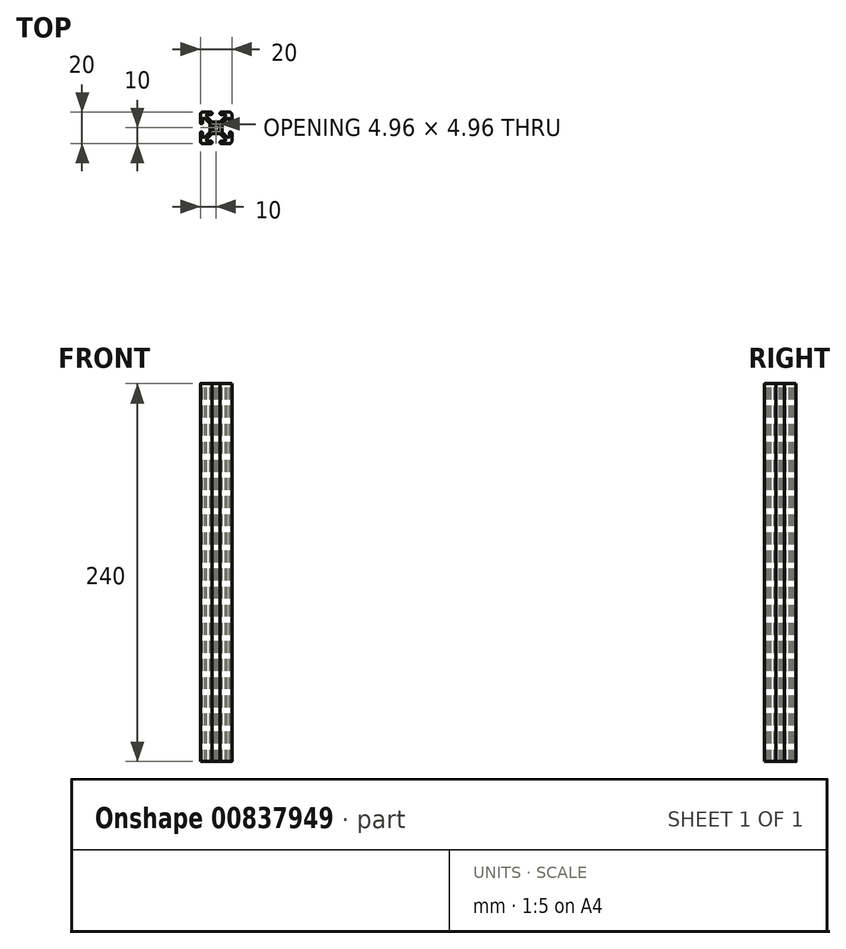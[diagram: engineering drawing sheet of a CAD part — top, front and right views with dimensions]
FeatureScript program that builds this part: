
annotation { "Feature Type Name" : "Feature", "Feature Type Description" : "" }
export const myFeature = defineFeature(function(context is Context, id is Id, definition is map)
    precondition{}
    {
        {
            var Q0;
            Q0=qCreatedBy(makeId("Top.planeOp"),FACE);
            var sketch = newSketch(context, id + "F0", { "sketchPlane" : qUnion([Q0])});
            skLineSegment(sketch, "E0.bottom", {"start": v(10, 10) * mm, "end": v(-10, 10) * mm});
            skLineSegment(sketch, "E0.top", {"start": v(10, -10) * mm, "end": v(-10, -10) * mm});
            skLineSegment(sketch, "E0.left", {"start": v(10, 10) * mm, "end": v(10, -10) * mm});
            skLineSegment(sketch, "E0.right", {"start": v(-10, 10) * mm, "end": v(-10, -10) * mm});
            skPoint(sketch, "E0.middle", {"position": v(0, 0) * mm});
            skCircle(sketch, "E1", {"center": v(0, 0) * mm, "radius": 2.1 * mm});
            skCircle(sketch, "E2", {"center": v(1.48, 1.48) * mm, "radius": 1 * mm});
            skLineSegment(sketch, "E3", {"start": v(0, 0) * mm, "end": v(1.48, 1.48) * mm, "construction": true});
            skLineSegment(sketch, "E4.bottom", {"start": v(-3.65, 3.65) * mm, "end": v(3.65, 3.65) * mm});
            skLineSegment(sketch, "E4.top", {"start": v(-3.65, -3.65) * mm, "end": v(3.65, -3.65) * mm});
            skLineSegment(sketch, "E4.left", {"start": v(-3.65, 3.65) * mm, "end": v(-3.65, -3.65) * mm});
            skLineSegment(sketch, "E4.right", {"start": v(3.65, 3.65) * mm, "end": v(3.65, -3.65) * mm});
            skCircle(sketch, "E5.1.0", {"center": v(-1.48, 1.48) * mm, "radius": 1 * mm});
            skCircle(sketch, "E5.2.0", {"center": v(-1.48, -1.48) * mm, "radius": 1 * mm});
            skCircle(sketch, "E5.3.0", {"center": v(1.48, -1.48) * mm, "radius": 1 * mm});
            skLineSegment(sketch, "E6.bottom", {"start": v(-8.5, 8.5) * mm, "end": v(8.5, 8.5) * mm});
            skLineSegment(sketch, "E6.top", {"start": v(-8.5, -8.5) * mm, "end": v(8.5, -8.5) * mm});
            skLineSegment(sketch, "E6.left", {"start": v(-8.5, 8.5) * mm, "end": v(-8.5, -8.5) * mm});
            skLineSegment(sketch, "E6.right", {"start": v(8.5, 8.5) * mm, "end": v(8.5, -8.5) * mm});
            skLineSegment(sketch, "E7", {"start": v(7.44, 8.5) * mm, "end": v(-8.5, -7.44) * mm});
            skLineSegment(sketch, "E8", {"start": v(-7.44, -8.5) * mm, "end": v(8.5, 7.44) * mm});
            skLineSegment(sketch, "E9", {"start": v(-8.5, 7.44) * mm, "end": v(7.44, -8.5) * mm});
            skLineSegment(sketch, "E10", {"start": v(8.5, -7.44) * mm, "end": v(-7.44, 8.5) * mm});
            skLineSegment(sketch, "E11", {"start": v(-10, 2.6) * mm, "end": v(-8.5, 2.6) * mm});
            skLineSegment(sketch, "E12", {"start": v(-10, -2.6) * mm, "end": v(-8.5, -2.6) * mm});
            skLineSegment(sketch, "E13", {"start": v(8.5, 2.6) * mm, "end": v(10, 2.6) * mm});
            skLineSegment(sketch, "E14", {"start": v(8.5, -2.6) * mm, "end": v(10, -2.6) * mm});
            skLineSegment(sketch, "E15", {"start": v(-2.6, 8.5) * mm, "end": v(-2.6, 10) * mm});
            skLineSegment(sketch, "E16", {"start": v(2.6, 8.5) * mm, "end": v(2.6, 10) * mm});
            skLineSegment(sketch, "E17", {"start": v(-2.6, -8.5) * mm, "end": v(-2.6, -10) * mm});
            skPoint(sketch, "E18.endSnap0", {"position": v(0, -10) * mm});
            skLineSegment(sketch, "E19", {"start": v(2.6, -8.5) * mm, "end": v(2.6, -10) * mm});
            skLineSegment(sketch, "E20", {"start": v(-8.5, 6) * mm, "end": v(-7.06, 6) * mm});
            skLineSegment(sketch, "E21", {"start": v(-6, 7.06) * mm, "end": v(-6, 8.5) * mm});
            skLineSegment(sketch, "E22", {"start": v(6, 8.5) * mm, "end": v(6, 7.06) * mm});
            skLineSegment(sketch, "E23", {"start": v(8.5, 6) * mm, "end": v(7.06, 6) * mm});
            skLineSegment(sketch, "E24", {"start": v(8.5, -6) * mm, "end": v(7.06, -6) * mm});
            skLineSegment(sketch, "E25", {"start": v(6, -8.5) * mm, "end": v(6, -7.06) * mm});
            skLineSegment(sketch, "E26", {"start": v(-6, -8.5) * mm, "end": v(-6, -7.06) * mm});
            skLineSegment(sketch, "E27", {"start": v(-7.06, -6) * mm, "end": v(-8.5, -6) * mm});
            skSolve(sketch);
        }
        {
            var Q0;
            {var subQ8=sQuery(id+"F0.wireOp",EDGE,"E11");Q0=makeQuery(id+"F0.imprint","IMPRINT",FACE,{"disambiguationData":[TD([[makeQuery(id+"F0.imprint","IMPRINT",EDGE,{"derivedFrom":subQ8}),1.0]])]});}
            var Q1;
            {var subQ3=sQuery(id+"F0.wireOp",EDGE,"E20");Q1=makeQuery(id+"F0.imprint","IMPRINT",FACE,{"disambiguationData":[TD([[makeQuery(id+"F0.imprint","IMPRINT",EDGE,{"derivedFrom":subQ3}),1.0]])]});}
            var Q2;
            {var subQ3=sQuery(id+"F0.wireOp",EDGE,"E21");Q2=makeQuery(id+"F0.imprint","IMPRINT",FACE,{"disambiguationData":[TD([[makeQuery(id+"F0.imprint","IMPRINT",EDGE,{"derivedFrom":subQ3}),1.0]])]});}
            var Q3;
            {var subQ5=sQuery(id+"F0.wireOp",EDGE,"E4.left");var subQ6=sQuery(id+"F0.wireOp",EDGE,"E4.bottom");var subQ7=makeQuery(id+"F0.imprint","INTERSECT",VERTEX,{"derivedFrom":[subQ6,subQ5]});Q3=makeQuery(id+"F0.imprint","IMPRINT",FACE,{"disambiguationData":[TD([[makeQuery(id+"F0.imprint","IMPRINT",EDGE,{"disambiguationData":[TD([[subQ7,-1.0]])],"derivedFrom":subQ6}),1.0]])]});}
            var Q4;
            {var subQ3=sQuery(id+"F0.wireOp",EDGE,"E13");Q4=makeQuery(id+"F0.imprint","IMPRINT",FACE,{"disambiguationData":[TD([[makeQuery(id+"F0.imprint","IMPRINT",EDGE,{"derivedFrom":subQ3}),1.0]])]});}
            var Q5;
            {var subQ3=sQuery(id+"F0.wireOp",EDGE,"E22");Q5=makeQuery(id+"F0.imprint","IMPRINT",FACE,{"disambiguationData":[TD([[makeQuery(id+"F0.imprint","IMPRINT",EDGE,{"derivedFrom":subQ3}),1.0]])]});}
            var Q6;
            {var subQ8=sQuery(id+"F0.wireOp",EDGE,"E4.right");var subQ9=sQuery(id+"F0.wireOp",EDGE,"E4.bottom");var subQ10=makeQuery(id+"F0.imprint","INTERSECT",VERTEX,{"derivedFrom":[subQ9,subQ8]});Q6=makeQuery(id+"F0.imprint","IMPRINT",FACE,{"disambiguationData":[TD([[makeQuery(id+"F0.imprint","IMPRINT",EDGE,{"disambiguationData":[TD([[subQ10,1.0]])],"derivedFrom":subQ9}),1.0]])]});}
            var Q7;
            {var subQ3=sQuery(id+"F0.wireOp",EDGE,"E23");Q7=makeQuery(id+"F0.imprint","IMPRINT",FACE,{"disambiguationData":[TD([[makeQuery(id+"F0.imprint","IMPRINT",EDGE,{"derivedFrom":subQ3}),-1.0]])]});}
            var Q8;
            {var subQ3=sQuery(id+"F0.wireOp",EDGE,"E25");Q8=makeQuery(id+"F0.imprint","IMPRINT",FACE,{"disambiguationData":[TD([[makeQuery(id+"F0.imprint","IMPRINT",EDGE,{"derivedFrom":subQ3}),-1.0]])]});}
            var Q9;
            {var subQ8=sQuery(id+"F0.wireOp",EDGE,"E4.right");var subQ10=sQuery(id+"F0.wireOp",EDGE,"E4.top");var subQ11=makeQuery(id+"F0.imprint","INTERSECT",VERTEX,{"derivedFrom":[subQ10,subQ8]});Q9=makeQuery(id+"F0.imprint","IMPRINT",FACE,{"disambiguationData":[TD([[makeQuery(id+"F0.imprint","IMPRINT",EDGE,{"disambiguationData":[TD([[subQ11,1.0]])],"derivedFrom":subQ10}),-1.0]])]});}
            var Q10;
            {var subQ3=sQuery(id+"F0.wireOp",EDGE,"E24");Q10=makeQuery(id+"F0.imprint","IMPRINT",FACE,{"disambiguationData":[TD([[makeQuery(id+"F0.imprint","IMPRINT",EDGE,{"derivedFrom":subQ3}),1.0]])]});}
            var Q11;
            {var subQ7=sQuery(id+"F0.wireOp",EDGE,"E14");Q11=makeQuery(id+"F0.imprint","IMPRINT",FACE,{"disambiguationData":[TD([[makeQuery(id+"F0.imprint","IMPRINT",EDGE,{"derivedFrom":subQ7}),-1.0]])]});}
            var Q12;
            {var subQ11=sQuery(id+"F0.wireOp",EDGE,"E12");Q12=makeQuery(id+"F0.imprint","IMPRINT",FACE,{"disambiguationData":[TD([[makeQuery(id+"F0.imprint","IMPRINT",EDGE,{"derivedFrom":subQ11}),-1.0]])]});}
            var Q13;
            {var subQ3=sQuery(id+"F0.wireOp",EDGE,"E26");Q13=makeQuery(id+"F0.imprint","IMPRINT",FACE,{"disambiguationData":[TD([[makeQuery(id+"F0.imprint","IMPRINT",EDGE,{"derivedFrom":subQ3}),1.0]])]});}
            var Q14;
            {var subQ3=sQuery(id+"F0.wireOp",EDGE,"E27");Q14=makeQuery(id+"F0.imprint","IMPRINT",FACE,{"disambiguationData":[TD([[makeQuery(id+"F0.imprint","IMPRINT",EDGE,{"derivedFrom":subQ3}),1.0]])]});}
            var Q15;
            {var subQ7=sQuery(id+"F0.wireOp",EDGE,"E4.top");var subQ11=sQuery(id+"F0.wireOp",EDGE,"E4.left");var subQ12=makeQuery(id+"F0.imprint","INTERSECT",VERTEX,{"derivedFrom":[subQ7,subQ11]});Q15=makeQuery(id+"F0.imprint","IMPRINT",FACE,{"disambiguationData":[TD([[makeQuery(id+"F0.imprint","IMPRINT",EDGE,{"disambiguationData":[TD([[subQ12,-1.0]])],"derivedFrom":subQ7}),-1.0]])]});}
            var Q16;
            {var subQ1=sQuery(id+"F0.wireOp",EDGE,"E4.left");var subQ7=sQuery(id+"F0.wireOp",EDGE,"E4.top");var subQ8=makeQuery(id+"F0.imprint","INTERSECT",VERTEX,{"derivedFrom":[subQ7,subQ1]});Q16=makeQuery(id+"F0.imprint","IMPRINT",FACE,{"disambiguationData":[TD([[makeQuery(id+"F0.imprint","IMPRINT",EDGE,{"disambiguationData":[TD([[subQ8,-1.0]])],"derivedFrom":subQ7}),1.0]])]});}
            var Q17;
            {var subQ1=sQuery(id+"F0.wireOp",EDGE,"E1");var subQ7=sQuery(id+"F0.wireOp",EDGE,"E5.2.0");var subQ8=makeQuery(id+"F0.imprint","INTERSECT",VERTEX,{"disambiguationData":[OD(1.0)],"derivedFrom":[subQ1,subQ7]});Q17=makeQuery(id+"F0.imprint","IMPRINT",FACE,{"disambiguationData":[TD([[makeQuery(id+"F0.imprint","IMPRINT",EDGE,{"disambiguationData":[TD([[subQ8,-1.0]])],"derivedFrom":subQ1}),-1.0]])]});}
            var Q18;
            {var subQ1=sQuery(id+"F0.wireOp",EDGE,"E4.top");var subQ7=sQuery(id+"F0.wireOp",EDGE,"E4.right");var subQ8=makeQuery(id+"F0.imprint","INTERSECT",VERTEX,{"derivedFrom":[subQ1,subQ7]});Q18=makeQuery(id+"F0.imprint","IMPRINT",FACE,{"disambiguationData":[TD([[makeQuery(id+"F0.imprint","IMPRINT",EDGE,{"disambiguationData":[TD([[subQ8,1.0]])],"derivedFrom":subQ1}),1.0]])]});}
            var Q19;
            {var subQ1=sQuery(id+"F0.wireOp",EDGE,"E1");var subQ9=sQuery(id+"F0.wireOp",EDGE,"E2");var subQ10=makeQuery(id+"F0.imprint","INTERSECT",VERTEX,{"disambiguationData":[OD(0.0)],"derivedFrom":[subQ1,subQ9]});Q19=makeQuery(id+"F0.imprint","IMPRINT",FACE,{"disambiguationData":[TD([[makeQuery(id+"F0.imprint","IMPRINT",EDGE,{"disambiguationData":[TD([[subQ10,1.0]])],"derivedFrom":subQ1}),-1.0]])]});}
            var Q20;
            {var subQ0=sQuery(id+"F0.wireOp",EDGE,"E7");var subQ1=sQuery(id+"F0.wireOp",EDGE,"E2");var subQ2=makeQuery(id+"F0.imprint","INTERSECT",VERTEX,{"disambiguationData":[OD(0.0)],"derivedFrom":[subQ1,subQ0]});Q20=makeQuery(id+"F0.imprint","IMPRINT",FACE,{"disambiguationData":[TD([[makeQuery(id+"F0.imprint","IMPRINT",EDGE,{"disambiguationData":[TD([[subQ2,1.0]])],"derivedFrom":subQ1}),-1.0]])]});}
            var Q21;
            {var subQ0=sQuery(id+"F0.wireOp",EDGE,"E2");var subQ1=sQuery(id+"F0.wireOp",EDGE,"E1");var subQ2=makeQuery(id+"F0.imprint","INTERSECT",VERTEX,{"disambiguationData":[OD(1.0)],"derivedFrom":[subQ1,subQ0]});Q21=makeQuery(id+"F0.imprint","IMPRINT",FACE,{"disambiguationData":[TD([[makeQuery(id+"F0.imprint","IMPRINT",EDGE,{"disambiguationData":[TD([[subQ2,-1.0]])],"derivedFrom":subQ1}),-1.0]])]});}
            var Q22;
            {var subQ5=sQuery(id+"F0.wireOp",EDGE,"E4.left");var subQ6=sQuery(id+"F0.wireOp",EDGE,"E4.bottom");var subQ7=makeQuery(id+"F0.imprint","INTERSECT",VERTEX,{"derivedFrom":[subQ6,subQ5]});Q22=makeQuery(id+"F0.imprint","IMPRINT",FACE,{"disambiguationData":[TD([[makeQuery(id+"F0.imprint","IMPRINT",EDGE,{"disambiguationData":[TD([[subQ7,-1.0]])],"derivedFrom":subQ6}),-1.0]])]});}
            var Q23;
            {var subQ1=sQuery(id+"F0.wireOp",EDGE,"E1");var subQ5=sQuery(id+"F0.wireOp",EDGE,"E5.1.0");var subQ6=makeQuery(id+"F0.imprint","INTERSECT",VERTEX,{"disambiguationData":[OD(1.0)],"derivedFrom":[subQ1,subQ5]});Q23=makeQuery(id+"F0.imprint","IMPRINT",FACE,{"disambiguationData":[TD([[makeQuery(id+"F0.imprint","IMPRINT",EDGE,{"disambiguationData":[TD([[subQ6,-1.0]])],"derivedFrom":subQ1}),-1.0]])]});}
            extrude(context, id + "F1", {"entities" : qUnion([Q0, Q1, Q2, Q3, Q4, Q5, Q6, Q7, Q8, Q9, Q10, Q11, Q12, Q13, Q14, Q15, Q16, Q17, Q18, Q19, Q20, Q21, Q22, Q23]), "depth" : -240 * mm, "offsetDistance" : 25 * mm});
        }
        {
            var Q0;
            Q0=makeQuery(id+"F1.opExtrude","SWEPT_EDGE",EDGE,{"disambiguationData":[OSD([sQuery(id+"F0.wireOp",EDGE,"E0.top"),sQuery(id+"F0.wireOp",EDGE,"E0.right")])]});
            var Q1;
            Q1=makeQuery(id+"F1.opExtrude","SWEPT_EDGE",EDGE,{"disambiguationData":[OSD([sQuery(id+"F0.wireOp",EDGE,"E0.bottom"),sQuery(id+"F0.wireOp",EDGE,"E0.right")])]});
            var Q2;
            Q2=makeQuery(id+"F1.opExtrude","SWEPT_EDGE",EDGE,{"disambiguationData":[OSD([sQuery(id+"F0.wireOp",EDGE,"E0.top"),sQuery(id+"F0.wireOp",EDGE,"E0.left")])]});
            var Q3;
            Q3=makeQuery(id+"F1.opExtrude","SWEPT_EDGE",EDGE,{"disambiguationData":[OSD([sQuery(id+"F0.wireOp",EDGE,"E0.bottom"),sQuery(id+"F0.wireOp",EDGE,"E0.left")])]});
            fillet(context, id + "F2", {"entities" : qUnion([Q0, Q1, Q2, Q3]), "radius" : 1.5 * mm, "tangentPropagation" : true, "allowEdgeOverflow" : false});
        }
        {
            var Q0;
            Q0=makeQuery(id+"F1.opExtrude","SWEPT_EDGE",EDGE,{"disambiguationData":[OSD([sQuery(id+"F0.wireOp",EDGE,"E6.top"),sQuery(id+"F0.wireOp",EDGE,"E26")])]});
            var Q1;
            Q1=makeQuery(id+"F1.opExtrude","SWEPT_EDGE",EDGE,{"disambiguationData":[OSD([sQuery(id+"F0.wireOp",EDGE,"E6.left"),sQuery(id+"F0.wireOp",EDGE,"E27")])]});
            var Q2;
            Q2=makeQuery(id+"F1.opExtrude","SWEPT_EDGE",EDGE,{"disambiguationData":[OSD([sQuery(id+"F0.wireOp",EDGE,"E6.left"),sQuery(id+"F0.wireOp",EDGE,"E20")])]});
            var Q3;
            Q3=makeQuery(id+"F1.opExtrude","SWEPT_EDGE",EDGE,{"disambiguationData":[OSD([sQuery(id+"F0.wireOp",EDGE,"E6.bottom"),sQuery(id+"F0.wireOp",EDGE,"E21")])]});
            var Q4;
            Q4=makeQuery(id+"F1.opExtrude","SWEPT_EDGE",EDGE,{"disambiguationData":[OSD([sQuery(id+"F0.wireOp",EDGE,"E6.top"),sQuery(id+"F0.wireOp",EDGE,"E25")])]});
            var Q5;
            Q5=makeQuery(id+"F1.opExtrude","SWEPT_EDGE",EDGE,{"disambiguationData":[OSD([sQuery(id+"F0.wireOp",EDGE,"E6.right"),sQuery(id+"F0.wireOp",EDGE,"E24")])]});
            var Q6;
            Q6=makeQuery(id+"F1.opExtrude","SWEPT_EDGE",EDGE,{"disambiguationData":[OSD([sQuery(id+"F0.wireOp",EDGE,"E6.right"),sQuery(id+"F0.wireOp",EDGE,"E23")])]});
            var Q7;
            Q7=makeQuery(id+"F1.opExtrude","SWEPT_EDGE",EDGE,{"disambiguationData":[OSD([sQuery(id+"F0.wireOp",EDGE,"E6.bottom"),sQuery(id+"F0.wireOp",EDGE,"E22")])]});
            var Q8;
            Q8=makeQuery(id+"F1.opExtrude","SWEPT_EDGE",EDGE,{"disambiguationData":[OSD([sQuery(id+"F0.wireOp",EDGE,"E0.bottom"),sQuery(id+"F0.wireOp",EDGE,"E15")])]});
            var Q9;
            Q9=makeQuery(id+"F1.opExtrude","SWEPT_EDGE",EDGE,{"disambiguationData":[OSD([sQuery(id+"F0.wireOp",EDGE,"E6.bottom"),sQuery(id+"F0.wireOp",EDGE,"E15")])]});
            var Q10;
            Q10=makeQuery(id+"F1.opExtrude","SWEPT_EDGE",EDGE,{"disambiguationData":[OSD([sQuery(id+"F0.wireOp",EDGE,"E0.bottom"),sQuery(id+"F0.wireOp",EDGE,"E16")])]});
            var Q11;
            Q11=makeQuery(id+"F1.opExtrude","SWEPT_EDGE",EDGE,{"disambiguationData":[OSD([sQuery(id+"F0.wireOp",EDGE,"E6.left"),sQuery(id+"F0.wireOp",EDGE,"E11")])]});
            var Q12;
            Q12=makeQuery(id+"F1.opExtrude","SWEPT_EDGE",EDGE,{"disambiguationData":[OSD([sQuery(id+"F0.wireOp",EDGE,"E6.left"),sQuery(id+"F0.wireOp",EDGE,"E12")])]});
            var Q13;
            Q13=makeQuery(id+"F1.opExtrude","SWEPT_EDGE",EDGE,{"disambiguationData":[OSD([sQuery(id+"F0.wireOp",EDGE,"E0.right"),sQuery(id+"F0.wireOp",EDGE,"E12")])]});
            var Q14;
            Q14=makeQuery(id+"F1.opExtrude","SWEPT_EDGE",EDGE,{"disambiguationData":[OSD([sQuery(id+"F0.wireOp",EDGE,"E6.top"),sQuery(id+"F0.wireOp",EDGE,"E17")])]});
            var Q15;
            Q15=makeQuery(id+"F1.opExtrude","SWEPT_EDGE",EDGE,{"disambiguationData":[OSD([sQuery(id+"F0.wireOp",EDGE,"E0.top"),sQuery(id+"F0.wireOp",EDGE,"E17")])]});
            var Q16;
            Q16=makeQuery(id+"F1.opExtrude","SWEPT_EDGE",EDGE,{"disambiguationData":[OSD([sQuery(id+"F0.wireOp",EDGE,"E6.top"),sQuery(id+"F0.wireOp",EDGE,"E19")])]});
            var Q17;
            Q17=makeQuery(id+"F1.opExtrude","SWEPT_EDGE",EDGE,{"disambiguationData":[OSD([sQuery(id+"F0.wireOp",EDGE,"E6.right"),sQuery(id+"F0.wireOp",EDGE,"E14")])]});
            var Q18;
            Q18=makeQuery(id+"F1.opExtrude","SWEPT_EDGE",EDGE,{"disambiguationData":[OSD([sQuery(id+"F0.wireOp",EDGE,"E0.left"),sQuery(id+"F0.wireOp",EDGE,"E14")])]});
            var Q19;
            Q19=makeQuery(id+"F1.opExtrude","SWEPT_EDGE",EDGE,{"disambiguationData":[OSD([sQuery(id+"F0.wireOp",EDGE,"E0.left"),sQuery(id+"F0.wireOp",EDGE,"E13")])]});
            var Q20;
            Q20=makeQuery(id+"F1.opExtrude","SWEPT_EDGE",EDGE,{"disambiguationData":[OSD([sQuery(id+"F0.wireOp",EDGE,"E6.right"),sQuery(id+"F0.wireOp",EDGE,"E13")])]});
            var Q21;
            Q21=makeQuery(id+"F1.opExtrude","SWEPT_EDGE",EDGE,{"disambiguationData":[OSD([sQuery(id+"F0.wireOp",EDGE,"E6.bottom"),sQuery(id+"F0.wireOp",EDGE,"E16")])]});
            var Q22;
            Q22=makeQuery(id+"F1.opExtrude","SWEPT_EDGE",EDGE,{"disambiguationData":[OSD([sQuery(id+"F0.wireOp",EDGE,"E0.right"),sQuery(id+"F0.wireOp",EDGE,"E11")])]});
            var Q23;
            Q23=makeQuery(id+"F1.opExtrude","SWEPT_EDGE",EDGE,{"disambiguationData":[OSD([sQuery(id+"F0.wireOp",EDGE,"E0.top"),sQuery(id+"F0.wireOp",EDGE,"E19")])]});
            fillet(context, id + "F3", {"entities" : qUnion([Q0, Q1, Q2, Q3, Q4, Q5, Q6, Q7, Q8, Q9, Q10, Q11, Q12, Q13, Q14, Q15, Q16, Q17, Q18, Q19, Q20, Q21, Q22, Q23]), "radius" : 0.5 * mm, "tangentPropagation" : true, "allowEdgeOverflow" : false});
        }
    });
